FCSTD DOCUMENT  (FreeCAD 0.19R21897 (Git))
Label: Assembly-2
License: cc-by-sa
LicenseURL: http://creativecommons.org/licenses/by-sa/4.0/
objects: App::Link×8, App::LinkElement×3, App::DocumentObjectGroup×2, PartDesign::CoordinateSystem×1, App::FeaturePython×1, App::Part×1, Spreadsheet::Sheet×1
note: 1 computed .brp shape members not serialized (recipe doc carries the construction recipe); baked Part::Feature solids carry a one-line shape summary decoded from their .brp
EXTERNAL_REF file=Frame2.FCStd obj=Part
EXTERNAL_REF file=Frame2.FCStd obj=Bearing1
EXTERNAL_REF file=Parts.FCStd obj=BearingHole
EXTERNAL_REF file=Parts.FCStd obj=Part001
EXTERNAL_REF file=Frame2.FCStd obj=Bearing2
EXTERNAL_REF file=Frame2.FCStd obj=CH1
EXTERNAL_REF file=Parts.FCStd obj=CH1
EXTERNAL_REF file=Parts.FCStd obj=Part
EXTERNAL_REF file=Parts.FCStd obj=BearingAxis001
EXTERNAL_REF file=Roller.FCStd obj=RollerAxis
EXTERNAL_REF file=Roller.FCStd obj=Part001
EXTERNAL_REF file=Parts.FCStd obj=CrankHex
EXTERNAL_REF file=Roller.FCStd obj=Hex
EXTERNAL_REF file=Parts.FCStd obj=Part002
EXTERNAL_REF file=Brace.FCStd obj=Bolt1
EXTERNAL_REF file=Frame2.FCStd obj=BraceFrameBolt
EXTERNAL_REF file=Brace.FCStd obj=Part

FEATURE [App::DocumentObjectGroup] Parts
FEATURE [PartDesign::CoordinateSystem] LCS_Origin
  AttacherType = Attacher::AttachEngine3D
  MapMode = 2
  Support = -> [X_Axis]
FEATURE [App::DocumentObjectGroup] Constraints
FEATURE [App::FeaturePython] Variables  # WARN: FeaturePython — macro-defined, semantics opaque (R4)
FEATURE [App::Link] Unnamed1_Frame  label="Frame"
  LinkedObject = -> <external Frame2.FCStd>#Part
FEATURE [App::Link] Parts_Bearing
  AssemblyType = Asm4EE
  AttachedBy = #BearingHole
  AttachedTo = Unnamed1_Frame#Bearing1
  AttachmentOffset = pos=(0,0,0) rot=(0,0,1;3.14159rad)
  LinkPlacement = pos=(-1029.1,-10.9985,818.462) rot=(0.694747,0.186157,0.694747;2.77349rad)
  LinkedObject = -> <external Parts.FCStd>#Part001
  Placement = pos=(-1029.1,-10.9985,818.462) rot=(0.694747,0.186157,0.694747;2.77349rad)
  expr: Placement = Unnamed1_Frame.Placement * Frame2#Bearing1.Placement * AttachmentOffset * Parts#BearingHole.Placement ^ -1
FEATURE [App::Link] Parts_Bearing001
  AssemblyType = Asm4EE
  AttachedBy = #BearingHole
  AttachedTo = Unnamed1_Frame#Bearing2
  AttachmentOffset = pos=(0,0,0) rot=(0,0,1;3.14159rad)
  LinkPlacement = pos=(1028.7,-10.9985,818.462) rot=(0.694747,0.186157,0.694747;2.77349rad)
  LinkedObject = -> <external Parts.FCStd>#Part001
  Placement = pos=(1028.7,-10.9985,818.462) rot=(0.694747,0.186157,0.694747;2.77349rad)
  expr: Placement = Unnamed1_Frame.Placement * Frame2#Bearing2.Placement * AttachmentOffset * Parts#BearingHole.Placement ^ -1
FEATURE [App::Link] Parts_Caster
  AssemblyType = Asm4EE
  AttachedBy = #CH1
  AttachedTo = Unnamed1_Frame#CH1
  AttachmentOffset = pos=(0,0,0) rot=(-0.707107,-0.707107,0;3.14159rad)
  LinkPlacement = pos=(-1079.5,-550.85,-25.4) rot=(0,0,1;1.5708rad)
  LinkedObject = -> <external Parts.FCStd>#Part
  Placement = pos=(-1079.5,-550.85,-25.4) rot=(0,0,1;1.5708rad)
  expr: Placement = Unnamed1_Frame.Placement * Frame2#CH1.Placement * AttachmentOffset * Parts#CH1.Placement ^ -1
FEATURE [App::LinkElement] Link_i0
  LinkPlacement = pos=(-9.28663e-05,810,3.8147e-07) rot=(0,0,1;0rad)
  LinkTransform = true
  LinkedObject = -> Parts_Caster
  Placement = pos=(-9.28663e-05,810,3.8147e-07) rot=(0,0,1;0rad)
FEATURE [App::LinkElement] Link_i1
  LinkPlacement = pos=(2159,0.00043365,3.8147e-07) rot=(0,0,1;0rad)
  LinkTransform = true
  LinkedObject = -> Parts_Caster
  Placement = pos=(2159,0.00043365,3.8147e-07) rot=(0,0,1;0rad)
FEATURE [App::LinkElement] Link_i2
  LinkPlacement = pos=(2159,797.001,3.8147e-07) rot=(0,0,1;0rad)
  LinkTransform = true
  LinkedObject = -> Parts_Caster
  Placement = pos=(2159,797.001,3.8147e-07) rot=(0,0,1;0rad)
FEATURE [App::Link] Link  label="Parts_Caster001"
  ElementCount = 3
  ElementList = -> [Link_i0,Link_i1,Link_i2]
  LinkTransform = true
  LinkedObject = -> Parts_Caster
FEATURE [App::Link] Roller_Part001
  AssemblyType = Asm4EE
  AttachedBy = #RollerAxis
  AttachedTo = Parts_Bearing#BearingAxis001
  AttachmentOffset = pos=(0,0,0) rot=(1,0,0;3.14159rad)
  LinkPlacement = pos=(-2.09862,-38.4948,834.337) rot=(-1,0,0;5.23599rad)
  LinkedObject = -> <external Roller.FCStd>#Part001
  Placement = pos=(-2.09862,-38.4948,834.337) rot=(-1,0,0;5.23599rad)
  expr: Placement = Parts_Bearing.Placement * Parts#BearingAxis001.Placement * AttachmentOffset * Roller#RollerAxis.Placement ^ -1
FEATURE [App::Link] Parts_Crank
  AssemblyType = Asm4EE
  AttachedBy = #CrankHex
  AttachedTo = Roller_Part001#Hex
  LinkPlacement = pos=(1120.04,-38.4948,834.337) rot=(-0.250563,-0.250563,-0.935113;1.63783rad)
  LinkedObject = -> <external Parts.FCStd>#Part002
  Placement = pos=(1120.04,-38.4948,834.337) rot=(-0.250563,-0.250563,-0.935113;1.63783rad)
  expr: Placement = Roller_Part001.Placement * Roller#Hex.Placement * AttachmentOffset * Parts#CrankHex.Placement ^ -1
FEATURE [App::Link] Unnamed_Frame
  AssemblyType = Asm4EE
  AttachedBy = #Bolt1
  AttachedTo = Unnamed1_Frame#BraceFrameBolt
  AttachmentOffset = pos=(0,0,0) rot=(0,0,1;3.14159rad)
  LinkPlacement = pos=(-0.482469,31.75,28.575) rot=(0,0,1;0rad)
  LinkedObject = -> <external Brace.FCStd>#Part
  Placement = pos=(-0.482469,31.75,28.575) rot=(0,0,1;0rad)
  expr: Placement = Unnamed1_Frame.Placement * Frame2#BraceFrameBolt.Placement * AttachmentOffset * Brace#Bolt1.Placement ^ -1
FEATURE [App::Part] Model
  Configuration = 0
  Group = -> [LCS_Origin,Constraints,Variables,Parts,Unnamed1_Frame,Parts_Bearing,Parts_Bearing001,Parts_Caster,Roller_Part001,Parts_Crank,Unnamed_Frame]
  Origin = -> Origin
  Type = Assembly4 Model
FEATURE [Spreadsheet::Sheet] Spreadsheet
  cells = A3=Frame; B4=1x3 Square Tube Steel; B5=2x3 square tube steel; B6=3/4" square stainless tube; B7=1" square stainless tube; B8=1/2" x 1/8" angle; B9=5/16" x 18 tpi  Rivnut; C9=16; B10=5/16" x 18 tpi x 3/4" bolt; C10=16; B11=9/16" x 1"  bolt; C11=4; B13=Caster w/Lock; C13=4; D13=Mcmaster-Carr; F13=https://www.mcmaster.com/2702t72; B14=3/4" flex head reversing wrench; C14=1; D14=Snap-on/Williams; F14=https://protoolwarehouse.com/3-4-williams-flex-head-reversible-ratcheting-comb-wrench-12-pt-1224rcf/; B15=Bearing; C15=2; D15=Mcmaster-Carr; E15=2820T9; F15=https://www.mcmaster.com/2820T9; B16=Crank; C16=1; D16=Mcmaster-carr; E16=6393K55; F16=https://www.mcmaster.com/6393K55; B17=2" x 3" plastic end caps; C17=4; A19=Roller; B20= 2" black iron gas pipe; C20=80 inch

RESOLVED EXTERNAL PARTS (link-assembly join: the EXTERNAL_REF files above that resolve inside this repo's crawl, each included once):
---- part Brace.FCStd = doc fcstd_0483c03d19d1 ----
FCSTD DOCUMENT  (FreeCAD 0.19R21120 (Git))
Label: Brace
License: All rights reserved
LicenseURL: http://en.wikipedia.org/wiki/All_rights_reserved
objects: Sketcher::SketchObject×8, PartDesign::Pad×4, PartDesign::Pocket×3, PartDesign::Body×3, App::Part×2, PartDesign::Mirrored×1, PartDesign::CoordinateSystem×1
note: 27 computed .brp shape members not serialized (recipe doc carries the construction recipe); baked Part::Feature solids carry a one-line shape summary decoded from their .brp

FEATURE [Sketcher::SketchObject] Sketch
  MapMode = 5
  Placement = pos=(0,0,0) rot=(0.57735,0.57735,0.57735;2.0944rad)
  Support = -> [YZ_Plane]
  sketch-geometry (8):
    g0: LineSegment StartX=-6.35 StartY=692.15 StartZ=0 EndX=6.35 EndY=692.15 EndZ=0
    g1: LineSegment StartX=6.35 StartY=692.15 StartZ=0 EndX=6.35 EndY=679.45 EndZ=0
    g2: LineSegment StartX=6.35 StartY=679.45 StartZ=0 EndX=-6.35 EndY=679.45 EndZ=0
    g3: LineSegment StartX=-6.35 StartY=679.45 StartZ=0 EndX=-6.35 EndY=692.15 EndZ=0
    g4: LineSegment StartX=-9.525 StartY=695.325 StartZ=0 EndX=9.525 EndY=695.325 EndZ=0
    g5: LineSegment StartX=9.525 StartY=695.325 StartZ=0 EndX=9.525 EndY=676.275 EndZ=0
    g6: LineSegment StartX=9.525 StartY=676.275 StartZ=0 EndX=-9.525 EndY=676.275 EndZ=0
    g7: LineSegment StartX=-9.525 StartY=676.275 StartZ=0 EndX=-9.525 EndY=695.325 EndZ=0
  constraints (23):
    c: Coincident(g0,g1)
    c: Coincident(g1,g2)
    c: Coincident(g2,g3)
    c: Coincident(g3,g0)
    c: Horizontal(g0)
    c: Horizontal(g2)
    c: Vertical(g1)
    c: Vertical(g3)
    c: Coincident(g4,g5)
    c: Coincident(g5,g6)
    c: Coincident(g6,g7)
    c: Coincident(g7,g4)
    c: Horizontal(g6)
    c: Vertical(g5)
    c: Vertical(g7)
    c: Symmetric(g4,g4,g-2)
    c: Equal(g4,g7)
    c: DistanceX(g2,g6) = -3.175
    c: DistanceY(g2,g6) = -3.175
    c: Equal(g3,g2)
    c: DistanceX(g0,g4) = 3.175
    c: DistanceX(g6,g6) = 19.05
    c: DistanceY(g5) = 676.275
FEATURE [PartDesign::Pad] Pad
  Length = 1041.4
  Length2 = 98.425
  Placement = pos=(0,0,0) rot=(0.57735,0.57735,0.57735;2.0944rad)
  Profile = -> Sketch
  Type = 0
FEATURE [Sketcher::SketchObject] Sketch001
  ExternalGeometry = -> [Pad]
  MapMode = 5
  Placement = pos=(-2.702e-13,3.86e-13,695.325) rot=(0,0,-1;1.5708rad)
  Support = -> [Pad]
  sketch-geometry (4):
    g0: LineSegment StartX=-6.35 StartY=1041.4 StartZ=0 EndX=9.525 EndY=1041.4 EndZ=0
    g1: LineSegment StartX=9.525 StartY=1041.4 StartZ=0 EndX=9.525 EndY=1016 EndZ=0
    g2: LineSegment StartX=9.525 StartY=1016 StartZ=0 EndX=-6.35 EndY=1016 EndZ=0
    g3: LineSegment StartX=-6.35 StartY=1016 StartZ=0 EndX=-6.35 EndY=1041.4 EndZ=0
  constraints (11):
    c: Coincident(g0,g1)
    c: Coincident(g1,g2)
    c: Coincident(g2,g3)
    c: Coincident(g3,g0)
    c: Horizontal(g0)
    c: Horizontal(g2)
    c: Vertical(g1)
    c: Vertical(g3)
    c: DistanceX(g-3,g0) = 3.175
    c: DistanceY(g3,g3) = 25.4
    c: Coincident(g0,g-3)
FEATURE [PartDesign::Pocket] Pocket
  BaseFeature = -> Pad
  Length = 6.35
  Length2 = 98.425
  Placement = pos=(0,0,0) rot=(0.57735,0.57735,0.57735;2.0944rad)
  Profile = -> Sketch001
  Type = 1
FEATURE [Sketcher::SketchObject] Sketch002
  ExternalGeometry = -> [Pocket]
  MapMode = 5
  Placement = pos=(2.8e-15,6.35,-4.2e-15) rot=(0.57735,0.57735,-0.57735;2.0944rad)
  Support = -> [Pocket]
  sketch-geometry (1):
    g0: Circle CenterX=-685.8 CenterY=1028.7 CenterZ=0 NormalX=0 NormalY=0 NormalZ=1 AngleXU=0 Radius=4.7625
  constraints (3):
    c: DistanceX(g0,g-3) = -9.525
    c: Diameter(g0) = 9.525
    c: DistanceY(g0) = 1028.7
FEATURE [PartDesign::Pocket] Pocket001
  BaseFeature = -> Pocket
  Length = 6.35
  Length2 = 98.425
  Placement = pos=(0,0,0) rot=(0.57735,0.57735,0.57735;2.0944rad)
  Profile = -> Sketch002
  Type = 1
FEATURE [PartDesign::Mirrored] Mirrored
  BaseFeature = -> Pocket001
  MirrorPlane = -> Sketch002 [H_Axis]
  Originals = -> [Pad,Pocket,Pocket001]
  Placement = pos=(0,0,0) rot=(0.57735,0.57735,0.57735;2.0944rad)
FEATURE [PartDesign::Body] Body  label="CrossBeam"
  Group = -> [Sketch,Pad,Sketch001,Pocket,Sketch002,Pocket001,Mirrored]
  Origin = -> Origin
  Tip = -> Mirrored
FEATURE [Sketcher::SketchObject] Sketch003
  MapMode = 5
  Placement = pos=(0,0,0) rot=(0.57735,0.57735,0.57735;2.0944rad)
  Support = -> [YZ_Plane001]
  sketch-geometry (9):
    g0: LineSegment StartX=-9.525 StartY=695.325 StartZ=0 EndX=9.525 EndY=695.325 EndZ=0
    g1: LineSegment StartX=9.525 StartY=695.325 StartZ=0 EndX=9.525 EndY=676.275 EndZ=0
    g2: LineSegment StartX=9.525 StartY=676.275 StartZ=0 EndX=-9.525 EndY=676.275 EndZ=0
    g3: LineSegment StartX=-9.525 StartY=676.275 StartZ=0 EndX=-9.525 EndY=695.325 EndZ=0
    g4: LineSegment StartX=-12.7 StartY=698.5 StartZ=0 EndX=12.7 EndY=698.5 EndZ=0
    g5: LineSegment StartX=12.7 StartY=698.5 StartZ=0 EndX=12.7 EndY=673.1 EndZ=0
    g6: LineSegment StartX=12.7 StartY=673.1 StartZ=0 EndX=-12.7 EndY=673.1 EndZ=0
    g7: LineSegment StartX=-12.7 StartY=673.1 StartZ=0 EndX=-12.7 EndY=698.5 EndZ=0
    g8: LineSegment [constr] StartX=-9.525 StartY=676.275 StartZ=0 EndX=-12.7 EndY=673.1 EndZ=0
  constraints (25):
    c: Coincident(g0,g1)
    c: Coincident(g1,g2)
    c: Coincident(g2,g3)
    c: Coincident(g3,g0)
    c: Horizontal(g0)
    c: Horizontal(g2)
    c: Vertical(g1)
    c: Vertical(g3)
    c: Coincident(g4,g5)
    c: Coincident(g5,g6)
    c: Coincident(g6,g7)
    c: Coincident(g7,g4)
    c: Horizontal(g6)
    c: Vertical(g5)
    c: Vertical(g7)
    c: Equal(g4,g7)
    c: Symmetric(g4,g4,g-2)
    c: DistanceX(g4,g4) = 25.4
    c: DistanceY(g1) = 676.275
    c: Equal(g0,g3)
    c: Coincident(g8,g2)
    c: Coincident(g8,g6)
    c: Angle(g6,g8) = 0.785398
    c: DistanceX(g6,g2) = 3.175
    c: DistanceY(g0,g4) = 3.175
FEATURE [PartDesign::Pad] Pad001
  Length = 203.2
  Length2 = 98.425
  Midplane = true
  Placement = pos=(0,0,0) rot=(0.57735,0.57735,0.57735;2.0944rad)
  Profile = -> Sketch003
  Type = 0
FEATURE [Sketcher::SketchObject] Sketch004
  ExternalGeometry = -> [Pad001]
  MapMode = 5
  Placement = pos=(-2.616e-13,3.736e-13,673.1) rot=(0.707107,0.707107,0;3.14159rad)
  Support = -> [Pad001]
  sketch-geometry (8):
    g0: LineSegment StartX=-9.525 StartY=9.525 StartZ=0 EndX=9.525 EndY=9.525 EndZ=0
    g1: LineSegment StartX=9.525 StartY=9.525 StartZ=0 EndX=9.525 EndY=-9.525 EndZ=0
    g2: LineSegment StartX=9.525 StartY=-9.525 StartZ=0 EndX=-9.525 EndY=-9.525 EndZ=0
    g3: LineSegment StartX=-9.525 StartY=-9.525 StartZ=0 EndX=-9.525 EndY=9.525 EndZ=0
    g4: LineSegment StartX=-6.35 StartY=6.35 StartZ=0 EndX=6.35 EndY=6.35 EndZ=0
    g5: LineSegment StartX=6.35 StartY=6.35 StartZ=0 EndX=6.35 EndY=-6.35 EndZ=0
    g6: LineSegment StartX=6.35 StartY=-6.35 StartZ=0 EndX=-6.35 EndY=-6.35 EndZ=0
    g7: LineSegment StartX=-6.35 StartY=-6.35 StartZ=0 EndX=-6.35 EndY=6.35 EndZ=0
  constraints (22):
    c: Coincident(g0,g1)
    c: Coincident(g1,g2)
    c: Coincident(g2,g3)
    c: Coincident(g3,g0)
    c: Horizontal(g0)
    c: Horizontal(g2)
    c: Vertical(g1)
    c: Vertical(g3)
    c: Coincident(g4,g5)
    c: Coincident(g5,g6)
    c: Coincident(g6,g7)
    c: Coincident(g7,g4)
    c: Horizontal(g4)
    c: Horizontal(g6)
    c: Vertical(g5)
    c: Vertical(g7)
    c: Symmetric(g0,g1,g-1)
    c: Equal(g0,g3)
    c: DistanceX(g0,g0) = 19.05
    c: Equal(g4,g5)
    c: Symmetric(g4,g5,g-1)
    c: DistanceX(g2,g6) = 3.175
FEATURE [PartDesign::Pad] Pad002
  BaseFeature = -> Pad001
  Length = 676.275
  Length2 = 98.425
  Placement = pos=(0,0,0) rot=(0.57735,0.57735,0.57735;2.0944rad)
  Profile = -> Sketch004
  Type = 0
FEATURE [Sketcher::SketchObject] Sketch005
  ExternalGeometry = -> [Pad002]
  MapMode = 5
  Placement = pos=(1.1e-15,-4e-16,-3.175) rot=(0.707107,0.707107,0;3.14159rad)
  Support = -> [Pad002]
  sketch-geometry (4):
    g0: LineSegment StartX=-2.38125 StartY=9.525 StartZ=0 EndX=2.38125 EndY=9.525 EndZ=0
    g1: LineSegment StartX=2.38125 StartY=9.525 StartZ=0 EndX=2.38125 EndY=-9.525 EndZ=0
    g2: LineSegment StartX=2.38125 StartY=-9.525 StartZ=0 EndX=-2.38125 EndY=-9.525 EndZ=0
    g3: LineSegment StartX=-2.38125 StartY=-9.525 StartZ=0 EndX=-2.38125 EndY=9.525 EndZ=0
  constraints (11):
    c: Coincident(g0,g1)
    c: Coincident(g1,g2)
    c: Coincident(g2,g3)
    c: Coincident(g3,g0)
    c: Horizontal(g0)
    c: Horizontal(g2)
    c: Vertical(g1)
    c: Vertical(g3)
    c: Symmetric(g0,g1,g-1)
    c: DistanceX(g0,g0) = 4.7625
    c: PointOnObject(g0,g-3)
FEATURE [PartDesign::Pocket] Pocket002
  BaseFeature = -> Pad002
  Length = 15.875
  Length2 = 98.425
  Placement = pos=(0,0,0) rot=(0.57735,0.57735,0.57735;2.0944rad)
  Profile = -> Sketch005
  Type = 0
FEATURE [PartDesign::Body] Body001  label="Carriage"
  Group = -> [Sketch003,Pad001,Sketch004,Pad002,Sketch005,Pocket002]
  Origin = -> Origin001
  Tip = -> Pocket002
FEATURE [PartDesign::CoordinateSystem] Bolt1
  AttacherType = Attacher::AttachEngine3D
  MapMode = 11
  Placement = pos=(-1028.7,6.35,685.8) rot=(0,0.707107,0.707107;3.14159rad)
  Support = -> [Mirrored]
FEATURE [App::Part] Part  label="Frame"
  Group = -> [Body,Body001,Bolt1]
  Origin = -> Origin002
FEATURE [Sketcher::SketchObject] Sketch006
  MapMode = 5
  Support = -> [XY_Plane004]
  sketch-geometry (8):
    g0: LineSegment StartX=-12.7 StartY=12.7 StartZ=0 EndX=12.7 EndY=12.7 EndZ=0
    g1: LineSegment StartX=12.7 StartY=12.7 StartZ=0 EndX=12.7 EndY=-12.7 EndZ=0
    g2: LineSegment StartX=12.7 StartY=-12.7 StartZ=0 EndX=-12.7 EndY=-12.7 EndZ=0
    g3: LineSegment StartX=-12.7 StartY=-12.7 StartZ=0 EndX=-12.7 EndY=12.7 EndZ=0
    g4: LineSegment StartX=-9.41787 StartY=9.41787 StartZ=0 EndX=9.41787 EndY=9.41787 EndZ=0
    g5: LineSegment StartX=9.41787 StartY=9.41787 StartZ=0 EndX=9.41787 EndY=-9.41787 EndZ=0
    g6: LineSegment StartX=9.41787 StartY=-9.41787 StartZ=0 EndX=-9.41787 EndY=-9.41787 EndZ=0
    g7: LineSegment StartX=-9.41787 StartY=-9.41787 StartZ=0 EndX=-9.41787 EndY=9.41787 EndZ=0
  constraints (22):
    c: Coincident(g0,g1)
    c: Coincident(g1,g2)
    c: Coincident(g2,g3)
    c: Coincident(g3,g0)
    c: Horizontal(g0)
    c: Horizontal(g2)
    c: Vertical(g1)
    c: Vertical(g3)
    c: Coincident(g4,g5)
    c: Coincident(g5,g6)
    c: Coincident(g6,g7)
    c: Coincident(g7,g4)
    c: Horizontal(g4)
    c: Horizontal(g6)
    c: Vertical(g5)
    c: Vertical(g7)
    c: Symmetric(g4,g6,g-1)
    c: Symmetric(g0,g2,g-1)
    c: Equal(g0,g3)
    c: Equal(g4,g7)
    c: DistanceX(g6,g2) = -3.28213
    c: DistanceX(g0,g0) = 25.4
FEATURE [PartDesign::Pad] Pad003
  Length = 203.2
  Length2 = 98.425
  Midplane = true
  Profile = -> Sketch006
  Type = 0
FEATURE [Sketcher::SketchObject] Sketch007
  MapMode = 5
  Placement = pos=(0,0,0) rot=(0.57735,0.57735,0.57735;2.0944rad)
  Support = -> [YZ_Plane004]
  sketch-geometry (5):
    g0: LineSegment StartX=-38.1 StartY=12.7 StartZ=0 EndX=-12.7 EndY=12.7 EndZ=0
    g1: LineSegment StartX=-12.7 StartY=12.7 StartZ=0 EndX=-12.7 EndY=-12.7 EndZ=0
    g2: LineSegment StartX=-12.7 StartY=-12.7 StartZ=0 EndX=-38.1 EndY=-12.7 EndZ=0
    g3: LineSegment StartX=-38.1 StartY=-12.7 StartZ=0 EndX=-38.1 EndY=12.7 EndZ=0
    g4: Circle CenterX=-25.4 CenterY=0 CenterZ=0 NormalX=0 NormalY=0 NormalZ=1 AngleXU=0 Radius=5.74957
  constraints (13):
    c: Coincident(g0,g1)
    c: Coincident(g1,g2)
    c: Coincident(g2,g3)
    c: Coincident(g3,g0)
    c: Horizontal(g0)
    c: Horizontal(g2)
    c: Vertical(g1)
    c: Vertical(g3)
    c: PointOnObject(g4,g-1)
    c: DistanceX(g0,g0) = 25.4
    c: Symmetric(g2,g0,g4)
    c: Equal(g0,g3)
    c: DistanceX(g0,g-1) = 12.7
FEATURE [PartDesign::Body] Body002
  Group = -> [Sketch006,Pad003,Sketch007]
  Origin = -> Origin004
  Tip = -> Pad003
FEATURE [App::Part] Part001
  Group = -> [Body002]
  Origin = -> Origin003
---- part Frame2.FCStd = doc fcstd_2e75a402df7f ----
FCSTD DOCUMENT  (FreeCAD 0.19R21897 (Git))
Label: Frame2
License: cc-by-sa
LicenseURL: http://creativecommons.org/licenses/by-sa/4.0/
objects: Sketcher::SketchObject×7, PartDesign::Pad×5, PartDesign::CoordinateSystem×4, PartDesign::Pocket×2, PartDesign::Body×2, PartDesign::SubShapeBinder×1, PartDesign::Plane×1, App::Link×1, PartDesign::Mirrored×1, PartDesign::MultiTransform×1, PartDesign::Fillet×1, Part::MultiFuse×1, App::Part×1
note: 34 computed .brp shape members not serialized (recipe doc carries the construction recipe); baked Part::Feature solids carry a one-line shape summary decoded from their .brp
EXTERNAL_REF file=MASTER2.FCStd obj=Body

FEATURE [Sketcher::SketchObject] Sketch
  MapMode = 5
  Placement = pos=(0,0,0) rot=(0.57735,0.57735,0.57735;2.0944rad)
  Support = -> [YZ_Plane]
  sketch-geometry (8):
    g0: LineSegment StartX=-38.1 StartY=25.4 StartZ=0 EndX=38.1 EndY=25.4 EndZ=0
    g1: LineSegment StartX=38.1 StartY=25.4 StartZ=0 EndX=38.1 EndY=-25.4 EndZ=0
    g2: LineSegment StartX=38.1 StartY=-25.4 StartZ=0 EndX=-38.1 EndY=-25.4 EndZ=0
    g3: LineSegment StartX=-38.1 StartY=-25.4 StartZ=0 EndX=-38.1 EndY=25.4 EndZ=0
    g4: LineSegment StartX=-36.6 StartY=23.9 StartZ=0 EndX=36.6 EndY=23.9 EndZ=0
    g5: LineSegment StartX=36.6 StartY=23.9 StartZ=0 EndX=36.6 EndY=-23.9 EndZ=0
    g6: LineSegment StartX=36.6 StartY=-23.9 StartZ=0 EndX=-36.6 EndY=-23.9 EndZ=0
    g7: LineSegment StartX=-36.6 StartY=-23.9 StartZ=0 EndX=-36.6 EndY=23.9 EndZ=0
  constraints (22):
    c: Coincident(g0,g1)
    c: Coincident(g1,g2)
    c: Coincident(g2,g3)
    c: Coincident(g3,g0)
    c: Horizontal(g0)
    c: Horizontal(g2)
    c: Vertical(g1)
    c: Vertical(g3)
    c: Symmetric(g2,g0,g-1)
    c: Coincident(g4,g5)
    c: Coincident(g5,g6)
    c: Coincident(g6,g7)
    c: Coincident(g7,g4)
    c: Horizontal(g4)
    c: Horizontal(g6)
    c: Vertical(g5)
    c: Vertical(g7)
    c: DistanceX(g2,g6) = 1.5
    c: DistanceY(g2,g6) = 1.5
    c: Symmetric(g4,g6,g-1)
    c: DistanceX(g0,g0) = 76.2
    c: DistanceY(g3,g3) = 50.8
FEATURE [PartDesign::Pad] Pad
  Length = 2085.34
  Length2 = 100
  Midplane = true
  Placement = pos=(0,0,0) rot=(0.57735,0.57735,0.57735;2.0944rad)
  Profile = -> Sketch
  Type = 0
FEATURE [PartDesign::SubShapeBinder] Binder
  BindMode = 0
  ClaimChildren = false
  Context = -> Part [Body.Binder.]
  Fuse = false
  MakeFace = true
  PartialLoad = false
  Relative = true
  Support = -> [<external MASTER2.FCStd>#Body[Sketch001.]]
  _Version = 2
FEATURE [PartDesign::Plane] DatumPlane
  AttachmentOffset = pos=(0,0,0) rot=(1,0,0;1.5708rad)
  Length = 1151.5
  MapMode = 49
  Placement = pos=(-1079.5,-609.6,-6.8e-14) rot=(1,0,0;1.5708rad)
  ResizeMode = 0
  Support = -> [Binder]
  Width = 97
FEATURE [Sketcher::SketchObject] Sketch001
  ExternalGeometry = -> [Binder]
  MapMode = 5
  Placement = pos=(-1079.5,-609.6,-6.8e-14) rot=(1,0,0;1.5708rad)
  Support = -> [DatumPlane]
  sketch-geometry (16):
    g0: LineSegment StartX=-36.6 StartY=23.9 StartZ=0 EndX=36.6 EndY=23.9 EndZ=0
    g1: LineSegment StartX=36.6 StartY=23.9 StartZ=0 EndX=36.6 EndY=-23.9 EndZ=0
    g2: LineSegment StartX=36.6 StartY=-23.9 StartZ=0 EndX=-36.6 EndY=-23.9 EndZ=0
    g3: LineSegment StartX=-36.6 StartY=-23.9 StartZ=0 EndX=-36.6 EndY=23.9 EndZ=0
    g4: LineSegment StartX=2122.4 StartY=23.9 StartZ=0 EndX=2195.6 EndY=23.9 EndZ=0
    g5: LineSegment StartX=2195.6 StartY=23.9 StartZ=0 EndX=2195.6 EndY=-23.9 EndZ=0
    g6: LineSegment StartX=2195.6 StartY=-23.9 StartZ=0 EndX=2122.4 EndY=-23.9 EndZ=0
    g7: LineSegment StartX=2122.4 StartY=-23.9 StartZ=0 EndX=2122.4 EndY=23.9 EndZ=0
    g8: LineSegment StartX=-38.1 StartY=25.4 StartZ=0 EndX=38.1 EndY=25.4 EndZ=0
    g9: LineSegment StartX=38.1 StartY=25.4 StartZ=0 EndX=38.1 EndY=-25.4 EndZ=0
    g10: LineSegment StartX=38.1 StartY=-25.4 StartZ=0 EndX=-38.1 EndY=-25.4 EndZ=0
    g11: LineSegment StartX=-38.1 StartY=-25.4 StartZ=0 EndX=-38.1 EndY=25.4 EndZ=0
    g12: LineSegment StartX=2120.9 StartY=25.4 StartZ=0 EndX=2197.1 EndY=25.4 EndZ=0
    g13: LineSegment StartX=2197.1 StartY=25.4 StartZ=0 EndX=2197.1 EndY=-25.4 EndZ=0
    g14: LineSegment StartX=2197.1 StartY=-25.4 StartZ=0 EndX=2120.9 EndY=-25.4 EndZ=0
    g15: LineSegment StartX=2120.9 StartY=-25.4 StartZ=0 EndX=2120.9 EndY=25.4 EndZ=0
  constraints (44):
    c: Coincident(g0,g1)
    c: Coincident(g1,g2)
    c: Coincident(g2,g3)
    c: Coincident(g3,g0)
    c: Horizontal(g0)
    c: Horizontal(g2)
    c: Vertical(g1)
    c: Vertical(g3)
    c: Coincident(g4,g5)
    c: Coincident(g5,g6)
    c: Coincident(g6,g7)
    c: Coincident(g7,g4)
    c: Horizontal(g4)
    c: Horizontal(g6)
    c: Vertical(g5)
    c: Vertical(g7)
    c: Symmetric(g6,g4,g-3)
    c: Symmetric(g0,g1,g-1)
    c: Equal(g4,g0)
    c: Equal(g3,g5)
    c: Coincident(g8,g9)
    c: Coincident(g9,g10)
    c: Coincident(g10,g11)
    c: Coincident(g11,g8)
    c: Horizontal(g8)
    c: Horizontal(g10)
    c: Vertical(g9)
    c: Vertical(g11)
    c: Symmetric(g8,g9,g-1)
    c: DistanceX(g10,g2) = 1.5
    c: DistanceY(g10,g2) = 1.5
    c: DistanceY(g11,g11) = 50.8
    c: DistanceX(g8,g8) = 76.2
    c: Coincident(g12,g13)
    c: Coincident(g13,g14)
    c: Coincident(g14,g15)
    c: Coincident(g15,g12)
    c: Horizontal(g12)
    c: Horizontal(g14)
    c: Vertical(g13)
    c: Vertical(g15)
    c: Symmetric(g12,g14,g-3)
    c: Equal(g12,g8)
    c: Equal(g15,g9)
FEATURE [PartDesign::Pad] Pad001
  BaseFeature = -> Pad
  Length = 914.4
  Length2 = 100
  Placement = pos=(0,0,0) rot=(0.57735,0.57735,0.57735;2.0944rad)
  Profile = -> Sketch001
  Reversed = true
  Type = 0
FEATURE [Sketcher::SketchObject] Sketch002
  MapMode = 5
  Placement = pos=(0,0,0) rot=(0.57735,0.57735,0.57735;2.0944rad)
  Support = -> [YZ_Plane001]
  sketch-geometry (4):
    g0: LineSegment StartX=38.1 StartY=878.103 StartZ=0 EndX=38.1 EndY=25.4 EndZ=0
    g1: LineSegment StartX=38.1 StartY=25.4 StartZ=0 EndX=-38.1 EndY=25.4 EndZ=0
    g2: LineSegment StartX=-38.1 StartY=25.4 StartZ=0 EndX=-38.1 EndY=746.121 EndZ=0
    g3: LineSegment StartX=38.1 StartY=878.103 StartZ=0 EndX=-38.1 EndY=746.121 EndZ=0
  constraints (11):
    c: Coincident(g0,g1)
    c: Coincident(g1,g2)
    c: Vertical(g0)
    c: Vertical(g2)
    c: DistanceX(g1,g1) = 76.2
    c: DistanceY(g1) = 25.4
    c: Coincident(g3,g0)
    c: Coincident(g3,g2)
    c: Angle(g3,g0) = 0.523599
    c: DistanceY(g0) = 878.103
    c: Symmetric(g1,g0,g-2)
FEATURE [PartDesign::Pad] Pad002
  Length = 25.4
  Length2 = 98.425
  Midplane = true
  Placement = pos=(0,0,0) rot=(0.57735,0.57735,0.57735;2.0944rad)
  Profile = -> Sketch002
  Type = 0
FEATURE [Sketcher::SketchObject] Sketch003
  ExternalGeometry = -> [Pad002]
  MapMode = 5
  Placement = pos=(-2.111e-13,-351.655,203.028) rot=(0.447214,0.447214,-0.774597;1.82348rad)
  Support = -> [Pad002]
  sketch-geometry (7):
    g0: Circle CenterX=-754.11 CenterY=-2.522e-13 CenterZ=0 NormalX=0 NormalY=0 NormalZ=1 AngleXU=0 Radius=6.35
    g1: Circle CenterX=-652.51 CenterY=-2.523e-13 CenterZ=0 NormalX=0 NormalY=0 NormalZ=1 AngleXU=0 Radius=6.35
    g2: LineSegment [constr] StartX=-652.51 StartY=-2.523e-13 StartZ=0 EndX=-754.11 EndY=-2.522e-13 EndZ=0
    g3: LineSegment StartX=-779.51 StartY=12.7 StartZ=0 EndX=-627.11 EndY=12.7 EndZ=0
    g4: LineSegment StartX=-627.11 StartY=12.7 StartZ=0 EndX=-627.11 EndY=-12.7 EndZ=0
    g5: LineSegment StartX=-627.11 StartY=-12.7 StartZ=0 EndX=-779.51 EndY=-12.7 EndZ=0
    g6: LineSegment StartX=-779.51 StartY=-12.7 StartZ=0 EndX=-779.51 EndY=12.7 EndZ=0
  constraints (16):
    c: DistanceX(g0,g1) = 101.6
    c: Equal(g0,g1)
    c: Diameter(g0) = 12.7
    c: Symmetric(g-3,g-3,g2)
    c: Coincident(g0,g2)
    c: Coincident(g2,g1)
    c: DistanceX(g-3,g0) = 25.4
    c: Coincident(g3,g4)
    c: Coincident(g4,g5)
    c: Coincident(g5,g6)
    c: Coincident(g6,g3)
    c: Horizontal(g5)
    c: Vertical(g4)
    c: Coincident(g3,g-4)
    c: Coincident(g3,g-4)
    c: Coincident(g5,g-3)
FEATURE [PartDesign::Pad] Pad003
  BaseFeature = -> Pad002
  Length = 12.7
  Length2 = 98.425
  Placement = pos=(0,0,0) rot=(0.57735,0.57735,0.57735;2.0944rad)
  Profile = -> Sketch003
  Type = 0
FEATURE [App::Link] Link  label="FrameUpright001"
  LinkPlacement = pos=(1028.7,0,0) rot=(0,0,1;0rad)
  LinkedObject = -> Body001
  Placement = pos=(1028.7,0,0) rot=(0,0,1;0rad)
FEATURE [Sketcher::SketchObject] Sketch004
  ExternalGeometry = -> [Pad001]
  MapMode = 5
  Placement = pos=(2.8e-15,-5.6e-15,-25.4) rot=(0.707107,0.707107,0;3.14159rad)
  Support = -> [Pad001]
  sketch-geometry (16):
    g0: LineSegment [constr] StartX=-588.95 StartY=-1057.28 StartZ=0 EndX=-512.75 EndY=-1057.28 EndZ=0
    g1: LineSegment [constr] StartX=-512.75 StartY=-1057.28 StartZ=0 EndX=-512.75 EndY=-1101.73 EndZ=0
    g2: LineSegment [constr] StartX=-512.75 StartY=-1101.73 StartZ=0 EndX=-588.95 EndY=-1101.73 EndZ=0
    g3: LineSegment [constr] StartX=-588.95 StartY=-1101.73 StartZ=0 EndX=-588.95 EndY=-1057.28 EndZ=0
    g4: Circle CenterX=-588.95 CenterY=-1057.28 CenterZ=0 NormalX=0 NormalY=0 NormalZ=1 AngleXU=0 Radius=3.96875
    g5: Circle CenterX=-512.75 CenterY=-1057.28 CenterZ=0 NormalX=0 NormalY=0 NormalZ=1 AngleXU=0 Radius=3.96875
    g6: Circle CenterX=-588.95 CenterY=-1101.73 CenterZ=0 NormalX=0 NormalY=0 NormalZ=1 AngleXU=0 Radius=3.96875
    g7: Circle CenterX=-512.75 CenterY=-1101.73 CenterZ=0 NormalX=0 NormalY=0 NormalZ=1 AngleXU=0 Radius=3.96875
    g8: LineSegment [constr] StartX=207.95 StartY=-1057.27 StartZ=0 EndX=284.15 EndY=-1057.27 EndZ=0
    g9: LineSegment [constr] StartX=284.15 StartY=-1057.27 StartZ=0 EndX=284.15 EndY=-1101.72 EndZ=0
    g10: LineSegment [constr] StartX=284.15 StartY=-1101.72 StartZ=0 EndX=207.95 EndY=-1101.72 EndZ=0
    g11: LineSegment [constr] StartX=207.95 StartY=-1101.72 StartZ=0 EndX=207.95 EndY=-1057.27 EndZ=0
    g12: Circle CenterX=207.95 CenterY=-1057.27 CenterZ=0 NormalX=0 NormalY=0 NormalZ=1 AngleXU=0 Radius=3.96875
    g13: Circle CenterX=207.95 CenterY=-1101.72 CenterZ=0 NormalX=0 NormalY=0 NormalZ=1 AngleXU=0 Radius=3.96875
    g14: Circle CenterX=284.15 CenterY=-1057.27 CenterZ=0 NormalX=0 NormalY=0 NormalZ=1 AngleXU=0 Radius=3.96875
    g15: Circle CenterX=284.15 CenterY=-1101.72 CenterZ=0 NormalX=0 NormalY=0 NormalZ=1 AngleXU=0 Radius=3.96875
  constraints (40):
    c: Coincident(g0,g1)
    c: Coincident(g1,g2)
    c: Coincident(g2,g3)
    c: Coincident(g3,g0)
    c: Horizontal(g0)
    c: Horizontal(g2)
    c: Vertical(g1)
    c: Vertical(g3)
    c: Coincident(g4,g0)
    c: Coincident(g5,g0)
    c: Coincident(g6,g2)
    c: Coincident(g7,g1)
    c: Equal(g4,g5)
    c: Equal(g5,g7)
    c: Equal(g7,g6)
    c: DistanceY(g3,g3) = 44.45
    c: DistanceX(g0,g0) = 76.2
    c: Diameter(g4) = 7.9375
    c: DistanceX(g4,g-3) = -20.6502
    c: DistanceY(g4,g-3) = -60.325
    c: Coincident(g8,g9)
    c: Coincident(g9,g10)
    c: Coincident(g10,g11)
    c: Coincident(g11,g8)
    c: Horizontal(g8)
    c: Horizontal(g10)
    c: Vertical(g9)
    c: Vertical(g11)
    c: Coincident(g12,g8)
    c: Coincident(g13,g10)
    c: Coincident(g14,g8)
    c: Coincident(g15,g9)
    c: Equal(g12,g14)
    c: Equal(g14,g13)
    c: Equal(g13,g15)
    c: Equal(g15,g4)
    c: Equal(g0,g8)
    c: Equal(g1,g11)
    c: PointOnObject(g12,g0)
    c: DistanceX(g15,g-4) = 20.6502
FEATURE [PartDesign::Pocket] Pocket
  BaseFeature = -> Pad001
  Length = 6.35
  Length2 = 98.425
  Placement = pos=(0,0,0) rot=(0.57735,0.57735,0.57735;2.0944rad)
  Profile = -> Sketch004
  Type = 0
FEATURE [PartDesign::Mirrored] Mirrored
  MirrorPlane = -> Sketch004 [H_Axis]
  Placement = pos=(0,0,0) rot=(0.57735,0.57735,0.57735;2.0944rad)
FEATURE [PartDesign::MultiTransform] MultiTransform
  BaseFeature = -> Pocket
  Originals = -> [Pocket]
  Placement = pos=(0,0,0) rot=(0.57735,0.57735,0.57735;2.0944rad)
  Transformations = -> [Mirrored]
FEATURE [PartDesign::CoordinateSystem] CH1
  AttacherType = Attacher::AttachEngine3D
  MapMode = 11
  Placement = pos=(-1101.73,-588.95,-25.4) rot=(1,0,0;3.14159rad)
  Support = -> [MultiTransform]
FEATURE [Sketcher::SketchObject] Sketch005
  MapMode = 5
  Placement = pos=(0,0,0) rot=(0.57735,0.57735,0.57735;2.0944rad)
  Support = -> [YZ_Plane]
  sketch-geometry (7):
    g0: LineSegment StartX=30.1625 StartY=38.1 StartZ=0 EndX=33.3375 EndY=38.1 EndZ=0
    g1: LineSegment StartX=33.3375 StartY=38.1 StartZ=0 EndX=33.3375 EndY=25.4 EndZ=0
    g2: LineSegment StartX=33.3375 StartY=25.4 StartZ=0 EndX=20.6375 EndY=25.4 EndZ=0
    g3: LineSegment StartX=20.6375 StartY=25.4 StartZ=0 EndX=20.6375 EndY=28.575 EndZ=0
    g4: LineSegment StartX=20.6375 StartY=28.575 StartZ=0 EndX=30.1625 EndY=28.575 EndZ=0
    g5: LineSegment StartX=30.1625 StartY=28.575 StartZ=0 EndX=30.1625 EndY=38.1 EndZ=0
    g6: GeomPoint X=31.75 Y=38.1 Z=0
  constraints (19):
    c: Horizontal(g0)
    c: Coincident(g0,g1)
    c: Vertical(g1)
    c: Coincident(g1,g2)
    c: Horizontal(g2)
    c: Coincident(g2,g3)
    c: Coincident(g3,g4)
    c: Horizontal(g4)
    c: Coincident(g4,g5)
    c: Coincident(g5,g0)
    c: Vertical(g5)
    c: Equal(g0,g3)
    c: Equal(g5,g4)
    c: Vertical(g3)
    c: DistanceX(g0,g0) = 3.175
    c: DistanceY(g2) = 25.4
    c: Symmetric(g0,g0,g6)
    c: DistanceX(g-1,g6) = 31.75
    c: DistanceY(g1,g1) = 12.7
FEATURE [PartDesign::Pad] Pad004
  BaseFeature = -> MultiTransform
  Length = 2032
  Length2 = 98.425
  Midplane = true
  Placement = pos=(0,0,0) rot=(0.57735,0.57735,0.57735;2.0944rad)
  Profile = -> Sketch005
  Type = 0
FEATURE [PartDesign::Body] Body  label="FrameBase"
  Group = -> [Binder,Sketch,Pad,DatumPlane,Sketch001,Pad001,Sketch004,Pocket,MultiTransform,Mirrored,Sketch005,Pad004]
  Origin = -> Origin
  Tip = -> Pad004
FEATURE [Sketcher::SketchObject] Sketch006
  ExternalGeometry = -> [Pad003]
  MapMode = 5
  Placement = pos=(1.68e-14,38.1,-8.4e-15) rot=(0.57735,0.57735,0.57735;4.18879rad)
  Support = -> [Pad003]
  sketch-geometry (1):
    g0: Circle CenterX=714.375 CenterY=-0.082469 CenterZ=0 NormalX=0 NormalY=0 NormalZ=1 AngleXU=0 Radius=3.175
  constraints (2):
    c: DistanceX(g-3,g0) = 688.975
    c: Diameter(g0) = 6.35
FEATURE [PartDesign::Pocket] Pocket001
  BaseFeature = -> Pad003
  Length = 6.35
  Length2 = 98.425
  Placement = pos=(0,0,0) rot=(0.57735,0.57735,0.57735;2.0944rad)
  Profile = -> Sketch006
  Type = 0
FEATURE [PartDesign::Fillet] Fillet
  Base = -> Pocket001 [Edge8]
  BaseFeature = -> Pocket001
  Placement = pos=(0,0,0) rot=(0.57735,0.57735,0.57735;2.0944rad)
  Radius = 12.446
  SupportTransform = true
FEATURE [PartDesign::Body] Body001  label="FrameUpright"
  Group = -> [Sketch002,Pad002,Sketch003,Pad003,Sketch006,Pocket001,Fillet]
  Origin = -> Origin001
  Placement = pos=(-1029.1,0,0) rot=(0,0,1;0rad)
  Tip = -> Fillet
FEATURE [Part::MultiFuse] Fusion
  Shapes = -> [Body,Body001,Link]
FEATURE [PartDesign::CoordinateSystem] Bearing1
  AttacherType = Attacher::AttachEngine3D
  MapMode = 11
  Placement = pos=(-1029.1,14.4015,862.456) rot=(1,0,0;1.0472rad)
  Support = -> [Fusion]
FEATURE [PartDesign::CoordinateSystem] Bearing2
  AttacherType = Attacher::AttachEngine3D
  MapMode = 11
  Placement = pos=(1028.7,14.4015,862.456) rot=(1,0,0;1.0472rad)
  Support = -> [Fusion]
FEATURE [PartDesign::CoordinateSystem] BraceFrameBolt
  AttacherType = Attacher::AttachEngine3D
  MapMode = 11
  Placement = pos=(-1029.18,38.1,714.375) rot=(-1,0,0;1.5708rad)
  Support = -> [Fusion]
FEATURE [App::Part] Part  label="Frame"
  Group = -> [Body001,Body,Link,Fusion,Bearing1,Bearing2,CH1,BraceFrameBolt]
  Origin = -> Origin002
---- part Roller.FCStd = doc fcstd_1ebb0c0061e0 ----
FCSTD DOCUMENT  (FreeCAD 0.19R21897 (Git))
Label: Roller
License: All rights reserved
LicenseURL: http://en.wikipedia.org/wiki/All_rights_reserved
objects: Sketcher::SketchObject×6, PartDesign::Pad×3, PartDesign::Body×3, App::Link×2, PartDesign::CoordinateSystem×2, PartDesign::Revolution×1, PartDesign::Pocket×1, PartDesign::Mirrored×1, Part::FeaturePython×1, App::Part×1
note: 23 computed .brp shape members not serialized (recipe doc carries the construction recipe); baked Part::Feature solids carry a one-line shape summary decoded from their .brp

FEATURE [Sketcher::SketchObject] Sketch003
  MapMode = 5
  Placement = pos=(0,0,0) rot=(0.57735,0.57735,0.57735;2.0944rad)
  Support = -> [YZ_Plane001]
  sketch-geometry (3):
    g0: Circle CenterX=0 CenterY=0 CenterZ=0 NormalX=0 NormalY=0 NormalZ=1 AngleXU=0 Radius=30.1625
    g1: Circle CenterX=0 CenterY=0 CenterZ=0 NormalX=0 NormalY=0 NormalZ=1 AngleXU=0 Radius=24.6253
    g2: LineSegment [constr] StartX=-30.1625 StartY=0 StartZ=0 EndX=-24.6253 EndY=0 EndZ=0
  constraints (8):
    c: Coincident(g0,g-1)
    c: Coincident(g1,g0)
    c: Diameter(g0) = 60.325
    c: PointOnObject(g2,g0)
    c: PointOnObject(g2,g1)
    c: Horizontal(g2)
    c: Perpendicular(g1,g2)
    c: DistanceX(g2,g2) = 5.5372
FEATURE [PartDesign::Pad] Pad
  Length = 2032
  Length2 = 100
  Midplane = true
  Placement = pos=(0,0,0) rot=(0.57735,0.57735,0.57735;2.0944rad)
  Profile = -> Sketch003
  Type = 0
FEATURE [PartDesign::Body] Body  label="Roller"
  Group = -> [Sketch003,Pad]
  Origin = -> Origin001
  Tip = -> Pad
FEATURE [Sketcher::SketchObject] Sketch004
  MapMode = 5
  Placement = pos=(0,0,0) rot=(0.57735,0.57735,0.57735;2.0944rad)
  Support = -> [YZ_Plane002]
  sketch-geometry (8):
    g0: LineSegment StartX=-12.7 StartY=14.7898 StartZ=0 EndX=-12.7 EndY=24.9779 EndZ=0
    g1: LineSegment StartX=-12.7 StartY=24.9779 StartZ=0 EndX=12.7 EndY=24.9779 EndZ=0
    g2: LineSegment StartX=12.7 StartY=24.9779 StartZ=0 EndX=12.7 EndY=14.7898 EndZ=0
    g3: LineSegment StartX=12.7 StartY=14.7898 StartZ=0 EndX=14.325 EndY=14.7898 EndZ=0
    g4: LineSegment StartX=14.325 StartY=14.7898 StartZ=0 EndX=14.325 EndY=26.5666 EndZ=0
    g5: LineSegment StartX=14.325 StartY=26.5666 StartZ=0 EndX=-14.325 EndY=26.5666 EndZ=0
    g6: LineSegment StartX=-14.325 StartY=26.5666 StartZ=0 EndX=-14.325 EndY=14.7898 EndZ=0
    g7: LineSegment StartX=-14.325 StartY=14.7898 StartZ=0 EndX=-12.7 EndY=14.7898 EndZ=0
  constraints (20):
    c: Coincident(g0,g1)
    c: Horizontal(g1)
    c: Coincident(g1,g2)
    c: Coincident(g2,g3)
    c: Horizontal(g3)
    c: Coincident(g3,g4)
    c: Coincident(g4,g5)
    c: Horizontal(g5)
    c: Coincident(g5,g6)
    c: Vertical(g6)
    c: Coincident(g6,g7)
    c: Coincident(g7,g0)
    c: Equal(g7,g3)
    c: Horizontal(g7)
    c: Vertical(g4)
    c: Vertical(g0)
    c: Symmetric(g2,g0,g-2)
    c: Vertical(g2)
    c: DistanceX(g1,g1) = 25.4
    c: DistanceX(g7,g7) = 1.625
FEATURE [PartDesign::Pad] Pad001
  Length = 2032
  Length2 = 100
  Midplane = true
  Placement = pos=(0,0,0) rot=(0.57735,0.57735,0.57735;2.0944rad)
  Profile = -> Sketch004
  Type = 0
FEATURE [Sketcher::SketchObject] Sketch005
  MapMode = 5
  Support = -> [XY_Plane003]
  sketch-geometry (6):
    g0: LineSegment StartX=39.4665 StartY=0 StartZ=0 EndX=39.4665 EndY=27.3939 EndZ=0
    g1: LineSegment StartX=39.4665 StartY=27.3939 StartZ=0 EndX=-36.7335 EndY=27.3939 EndZ=0
    g2: LineSegment StartX=-36.7335 StartY=27.3939 StartZ=0 EndX=-36.7335 EndY=12.7 EndZ=0
    g3: LineSegment StartX=-36.7335 StartY=12.7 StartZ=0 EndX=-93.8835 EndY=12.7 EndZ=0
    g4: LineSegment StartX=-93.8835 StartY=12.7 StartZ=0 EndX=-93.8835 EndY=0 EndZ=0
    g5: LineSegment StartX=-93.8835 StartY=0 StartZ=0 EndX=39.4665 EndY=0 EndZ=0
  constraints (17):
    c: PointOnObject(g0,g-1)
    c: Vertical(g0)
    c: Coincident(g0,g1)
    c: Horizontal(g1)
    c: Coincident(g1,g2)
    c: Coincident(g2,g3)
    c: Horizontal(g3)
    c: Coincident(g3,g4)
    c: PointOnObject(g4,g-1)
    c: Vertical(g4)
    c: Coincident(g4,g5)
    c: Coincident(g5,g0)
    c: Vertical(g2)
    c: DistanceY(g0,g0) = 27.3939
    c: DistanceX(g1,g1) = 76.2
    c: DistanceY(g4,g4) = 12.7
    c: DistanceX(g3,g3) = 57.15
FEATURE [PartDesign::Revolution] Revolution
  Angle = 360
  Axis = (1,0,0)
  Base = (0,0,0)
  Profile = -> Sketch005
  ReferenceAxis = -> Sketch005 [H_Axis]
FEATURE [Sketcher::SketchObject] Sketch006
  MapMode = 5
  Placement = pos=(-93.8835,0,0) rot=(0.57735,-0.57735,-0.57735;2.0944rad)
  Support = -> [Revolution]
FEATURE [Sketcher::SketchObject] Sketch007
  MapMode = 5
  Placement = pos=(-93.8835,0,0) rot=(0.57735,-0.57735,-0.57735;2.0944rad)
  Support = -> [Revolution]
  sketch-geometry (7):
    g0: LineSegment StartX=8.24889 StartY=-4.7625 StartZ=0 EndX=8.24889 EndY=4.7625 EndZ=0
    g1: LineSegment StartX=8.24889 StartY=4.7625 StartZ=0 EndX=0 EndY=9.525 EndZ=0
    g2: LineSegment StartX=0 StartY=9.525 StartZ=0 EndX=-8.24889 EndY=4.7625 EndZ=0
    g3: LineSegment StartX=-8.24889 StartY=4.7625 StartZ=0 EndX=-8.24889 EndY=-4.7625 EndZ=0
    g4: LineSegment StartX=-8.24889 StartY=-4.7625 StartZ=0 EndX=7.681e-12 EndY=-9.525 EndZ=0
    g5: LineSegment StartX=7.681e-12 StartY=-9.525 StartZ=0 EndX=8.24889 EndY=-4.7625 EndZ=0
    g6: Circle [constr] CenterX=0 CenterY=0 CenterZ=0 NormalX=0 NormalY=0 NormalZ=1 AngleXU=0 Radius=9.525
  constraints (16):
    c: Coincident(g0,g1)
    c: Coincident(g1,g2)
    c: Coincident(g2,g3)
    c: Coincident(g3,g4)
    c: Coincident(g4,g5)
    c: Coincident(g5,g0)
    c: Equal(g0, g1-g5) x5
    c: PointOnObject(g0,g6)
    c: PointOnObject(g1,g6)
    c: PointOnObject(g2,g6)
    c: PointOnObject(g3,g6)
    c: PointOnObject(g4,g6)
    c: PointOnObject(g5,g6)
    c: Coincident(g6,g-1)
    c: Diameter(g6) = 19.05
    c: PointOnObject(g1,g-2)
FEATURE [PartDesign::Pad] Pad002
  BaseFeature = -> Revolution
  Length = 50
  Length2 = 100
  Profile = -> Sketch007
  Type = 0
FEATURE [PartDesign::Body] Body002  label="BearingHub001"
  Group = -> [Sketch005,Revolution,Sketch006,Sketch007,Pad002]
  Origin = -> Origin003
  Placement = pos=(-979.17,0,0) rot=(0,0,1;0rad)
  Tip = -> Pad002
FEATURE [App::Link] Link002  label="BearingHub"
  LinkPlacement = pos=(979.17,0,0) rot=(0,0,1;3.14159rad)
  LinkedObject = -> Body002
  Placement = pos=(979.17,0,0) rot=(0,0,1;3.14159rad)
FEATURE [PartDesign::CoordinateSystem] RollerAxis
  AttacherType = Attacher::AttachEngine3D
  MapMode = 11
  Placement = pos=(-1016,4.547e-13,-2.82e-13) rot=(0.707107,0,0.707107;3.14159rad)
  Support = -> [Pad]
FEATURE [PartDesign::CoordinateSystem] Hex
  AttacherType = Attacher::AttachEngine3D
  AttachmentOffset = pos=(0,0,1193.8) rot=(0,0,1;0rad)
  MapMode = 11
  Placement = pos=(1099.92,0,-2.651e-13) rot=(0.707107,0,0.707107;3.14159rad)
  Support = -> [Pad002]
FEATURE [Sketcher::SketchObject] Sketch
  MapMode = 5
  Placement = pos=(-7.4e-15,1.17e-14,26.5666) rot=(0,0,-1;1.5708rad)
  Support = -> [Pad001]
  sketch-geometry (1):
    g0: Circle CenterX=0 CenterY=990.6 CenterZ=0 NormalX=0 NormalY=0 NormalZ=1 AngleXU=0 Radius=3.96875
  constraints (3):
    c: PointOnObject(g0,g-2)
    c: Diameter(g0) = 7.9375
    c: DistanceY(g0) = 990.6
FEATURE [PartDesign::Pocket] Pocket
  BaseFeature = -> Pad001
  Length = 6.35
  Length2 = 98.425
  Placement = pos=(0,0,0) rot=(0.57735,0.57735,0.57735;2.0944rad)
  Profile = -> Sketch
  Type = 0
FEATURE [PartDesign::Mirrored] Mirrored
  BaseFeature = -> Pocket
  MirrorPlane = -> Sketch [H_Axis]
  Originals = -> [Pocket]
  Placement = pos=(0,0,0) rot=(0.57735,0.57735,0.57735;2.0944rad)
FEATURE [PartDesign::Body] Body001  label="ClampChannel"
  Group = -> [Sketch004,Pad001,Sketch,Pocket,Mirrored]
  Origin = -> Origin002
  Placement = pos=(0,0,19.05) rot=(0,0,1;0rad)
  Tip = -> Mirrored
FEATURE [Part::FeaturePython] Screw  label="M6x79.375-Screw"  # Fasteners workbench fastener (typed FeaturePython)
  Placement = pos=(991,0,69) rot=(0,0,1;0rad)
  diameter = 8
  invert = false
  length = 14
  lengthCustom = 79.375
  matchOuter = false
  offset = 0
  thread = false
  type = 14
FEATURE [App::Link] Link  label="1/4x20tpi-screw2"
  LinkPlacement = pos=(-990.4,1.10865e-05,69.85) rot=(0,0,1;0rad)
  LinkedObject = -> Screw
  Placement = pos=(-990.4,1.10865e-05,69.85) rot=(0,0,1;0rad)
FEATURE [App::Part] Part001
  Group = -> [Link002,Body,Body001,Body002,RollerAxis,Hex,Screw,Link]
  Origin = -> Origin004
